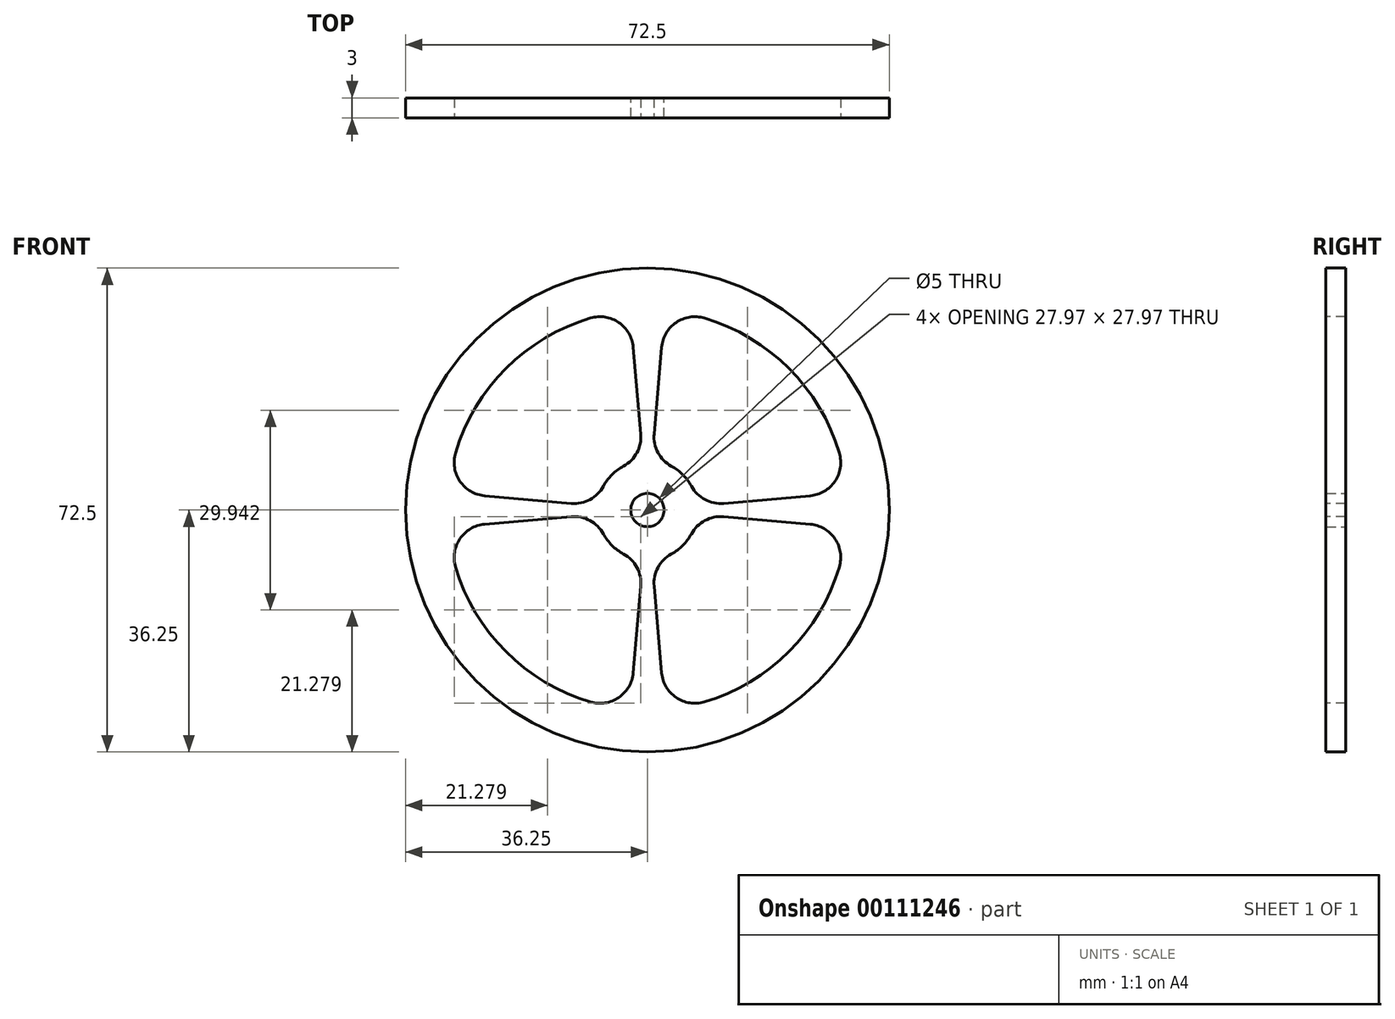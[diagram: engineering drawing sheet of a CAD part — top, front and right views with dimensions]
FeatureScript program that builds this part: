
annotation { "Feature Type Name" : "Feature", "Feature Type Description" : "" }
export const myFeature = defineFeature(function(context is Context, id is Id, definition is map)
    precondition{}
    {
        {
            var Q0;
            Q0=qCreatedBy(makeId("Front.planeOp"),FACE);
            var sketch = newSketch(context, id + "F0", { "sketchPlane" : qUnion([Q0])});
            skCircle(sketch, "E0", {"center": v(0, 0) * mm, "radius": 36.25 * mm});
            skCircle(sketch, "E1", {"center": v(0, 0) * mm, "radius": 2.5 * mm});
            skSolve(sketch);
        }
        {
            var Q0;
            Q0 = qSketchRegion(id + "F0", true);
            extrude(context, id + "F1", {"entities" : qUnion([Q0]), "depth" : 3 * mm});
        }
        {
            var Q0;
            Q0=makeQuery(id+"F1.opExtrude","CAP_FACE",FACE,{"disambiguationData":[OSD([sQuery(id+"F0.wireOp",EDGE,"E0"),sQuery(id+"F0.wireOp",EDGE,"E1")])],"isStart":false});
            var sketch = newSketch(context, id + "F2", { "sketchPlane" : qUnion([Q0])});
            skCircle(sketch, "E2", {"center": v(0, 0) * mm, "radius": 30 * mm});
            skCircle(sketch, "E3", {"center": v(0, 0) * mm, "radius": 7.5 * mm});
            skLineSegment(sketch, "E4", {"start": v(7.47, 0.65) * mm, "end": v(29.89, 2.61) * mm});
            skLineSegment(sketch, "E5", {"start": v(0.65, 7.47) * mm, "end": v(2.61, 29.89) * mm});
            skLineSegment(sketch, "E6", {"start": v(-0.65, 7.47) * mm, "end": v(-2.61, 29.89) * mm});
            skLineSegment(sketch, "E7", {"start": v(-7.47, 0.65) * mm, "end": v(-29.89, 2.61) * mm});
            skLineSegment(sketch, "E8", {"start": v(-7.47, -0.65) * mm, "end": v(-29.89, -2.61) * mm});
            skLineSegment(sketch, "E9", {"start": v(-0.65, -7.47) * mm, "end": v(-2.61, -29.89) * mm});
            skLineSegment(sketch, "E10", {"start": v(0.65, -7.47) * mm, "end": v(2.61, -29.89) * mm});
            skLineSegment(sketch, "E11", {"start": v(7.47, -0.65) * mm, "end": v(29.89, -2.61) * mm});
            skSolve(sketch);
        }
        {
            var Q0;
            {var subQ0=sQuery(id+"F2.wireOp",EDGE,"E8");Q0=makeQuery(id+"F2.imprint","IMPRINT",FACE,{"disambiguationData":[TD([[makeQuery(id+"F2.imprint","IMPRINT",EDGE,{"derivedFrom":subQ0}),1.0]])]});}
            var Q1;
            {var subQ0=sQuery(id+"F2.wireOp",EDGE,"E6");Q1=makeQuery(id+"F2.imprint","IMPRINT",FACE,{"disambiguationData":[TD([[makeQuery(id+"F2.imprint","IMPRINT",EDGE,{"derivedFrom":subQ0}),1.0]])]});}
            var Q2;
            {var subQ0=sQuery(id+"F2.wireOp",EDGE,"E4");Q2=makeQuery(id+"F2.imprint","IMPRINT",FACE,{"disambiguationData":[TD([[makeQuery(id+"F2.imprint","IMPRINT",EDGE,{"derivedFrom":subQ0}),1.0]])]});}
            var Q3;
            {var subQ0=sQuery(id+"F2.wireOp",EDGE,"E10");Q3=makeQuery(id+"F2.imprint","IMPRINT",FACE,{"disambiguationData":[TD([[makeQuery(id+"F2.imprint","IMPRINT",EDGE,{"derivedFrom":subQ0}),1.0]])]});}
            extrude(context, id + "F3", {"entities" : qUnion([Q0, Q1, Q2, Q3]), "operationType" : NewBodyOperationType.REMOVE, "oppositeDirection" : true, "depth" : 25 * mm});
        }
        {
            var Q0;
            Q0=makeQuery(id+"F3.boolean.opBoolean","COPY",EDGE,{"derivedFrom":makeQuery(id+"F3.opExtrude","SWEPT_EDGE",EDGE,{"disambiguationData":[OSD([sQuery(id+"F2.wireOp",EDGE,"E3"),sQuery(id+"F2.wireOp",EDGE,"E6")])]})});
            var Q1;
            Q1=makeQuery(id+"F3.boolean.opBoolean","COPY",EDGE,{"derivedFrom":makeQuery(id+"F3.opExtrude","SWEPT_EDGE",EDGE,{"disambiguationData":[OSD([sQuery(id+"F2.wireOp",EDGE,"E3"),sQuery(id+"F2.wireOp",EDGE,"E7")])]})});
            var Q2;
            Q2=makeQuery(id+"F3.boolean.opBoolean","COPY",EDGE,{"derivedFrom":makeQuery(id+"F3.opExtrude","SWEPT_EDGE",EDGE,{"disambiguationData":[OSD([sQuery(id+"F2.wireOp",EDGE,"E3"),sQuery(id+"F2.wireOp",EDGE,"E11")])]})});
            var Q3;
            Q3=makeQuery(id+"F3.boolean.opBoolean","COPY",EDGE,{"derivedFrom":makeQuery(id+"F3.opExtrude","SWEPT_EDGE",EDGE,{"disambiguationData":[OSD([sQuery(id+"F2.wireOp",EDGE,"E3"),sQuery(id+"F2.wireOp",EDGE,"E10")])]})});
            var Q4;
            Q4=makeQuery(id+"F3.boolean.opBoolean","COPY",EDGE,{"derivedFrom":makeQuery(id+"F3.opExtrude","SWEPT_EDGE",EDGE,{"disambiguationData":[OSD([sQuery(id+"F2.wireOp",EDGE,"E3"),sQuery(id+"F2.wireOp",EDGE,"E8")])]})});
            var Q5;
            Q5=makeQuery(id+"F3.boolean.opBoolean","COPY",EDGE,{"derivedFrom":makeQuery(id+"F3.opExtrude","SWEPT_EDGE",EDGE,{"disambiguationData":[OSD([sQuery(id+"F2.wireOp",EDGE,"E3"),sQuery(id+"F2.wireOp",EDGE,"E9")])]})});
            var Q6;
            Q6=makeQuery(id+"F3.boolean.opBoolean","COPY",EDGE,{"derivedFrom":makeQuery(id+"F3.opExtrude","SWEPT_EDGE",EDGE,{"disambiguationData":[OSD([sQuery(id+"F2.wireOp",EDGE,"E3"),sQuery(id+"F2.wireOp",EDGE,"E5")])]})});
            var Q7;
            Q7=makeQuery(id+"F3.boolean.opBoolean","COPY",EDGE,{"derivedFrom":makeQuery(id+"F3.opExtrude","SWEPT_EDGE",EDGE,{"disambiguationData":[OSD([sQuery(id+"F2.wireOp",EDGE,"E3"),sQuery(id+"F2.wireOp",EDGE,"E4")])]})});
            var Q8;
            Q8=makeQuery(id+"F3.boolean.opBoolean","COPY",EDGE,{"derivedFrom":makeQuery(id+"F3.opExtrude","SWEPT_EDGE",EDGE,{"disambiguationData":[OSD([sQuery(id+"F2.wireOp",EDGE,"E2"),sQuery(id+"F2.wireOp",EDGE,"E5")])]})});
            var Q9;
            Q9=makeQuery(id+"F3.boolean.opBoolean","COPY",EDGE,{"derivedFrom":makeQuery(id+"F3.opExtrude","SWEPT_EDGE",EDGE,{"disambiguationData":[OSD([sQuery(id+"F2.wireOp",EDGE,"E2"),sQuery(id+"F2.wireOp",EDGE,"E8")])]})});
            var Q10;
            Q10=makeQuery(id+"F3.boolean.opBoolean","COPY",EDGE,{"derivedFrom":makeQuery(id+"F3.opExtrude","SWEPT_EDGE",EDGE,{"disambiguationData":[OSD([sQuery(id+"F2.wireOp",EDGE,"E2"),sQuery(id+"F2.wireOp",EDGE,"E11")])]})});
            var Q11;
            Q11=makeQuery(id+"F3.boolean.opBoolean","COPY",EDGE,{"derivedFrom":makeQuery(id+"F3.opExtrude","SWEPT_EDGE",EDGE,{"disambiguationData":[OSD([sQuery(id+"F2.wireOp",EDGE,"E2"),sQuery(id+"F2.wireOp",EDGE,"E9")])]})});
            var Q12;
            Q12=makeQuery(id+"F3.boolean.opBoolean","COPY",EDGE,{"derivedFrom":makeQuery(id+"F3.opExtrude","SWEPT_EDGE",EDGE,{"disambiguationData":[OSD([sQuery(id+"F2.wireOp",EDGE,"E2"),sQuery(id+"F2.wireOp",EDGE,"E4")])]})});
            var Q13;
            Q13=makeQuery(id+"F3.boolean.opBoolean","COPY",EDGE,{"derivedFrom":makeQuery(id+"F3.opExtrude","SWEPT_EDGE",EDGE,{"disambiguationData":[OSD([sQuery(id+"F2.wireOp",EDGE,"E2"),sQuery(id+"F2.wireOp",EDGE,"E7")])]})});
            var Q14;
            Q14=makeQuery(id+"F3.boolean.opBoolean","COPY",EDGE,{"derivedFrom":makeQuery(id+"F3.opExtrude","SWEPT_EDGE",EDGE,{"disambiguationData":[OSD([sQuery(id+"F2.wireOp",EDGE,"E2"),sQuery(id+"F2.wireOp",EDGE,"E10")])]})});
            var Q15;
            Q15=makeQuery(id+"F3.boolean.opBoolean","COPY",EDGE,{"derivedFrom":makeQuery(id+"F3.opExtrude","SWEPT_EDGE",EDGE,{"disambiguationData":[OSD([sQuery(id+"F2.wireOp",EDGE,"E2"),sQuery(id+"F2.wireOp",EDGE,"E6")])]})});
            fillet(context, id + "F4", {"entities" : qUnion([Q0, Q1, Q2, Q3, Q4, Q5, Q6, Q7, Q8, Q9, Q10, Q11, Q12, Q13, Q14, Q15]), "radius" : 5 * mm, "tangentPropagation" : true, "allowEdgeOverflow" : false});
        }
    });
